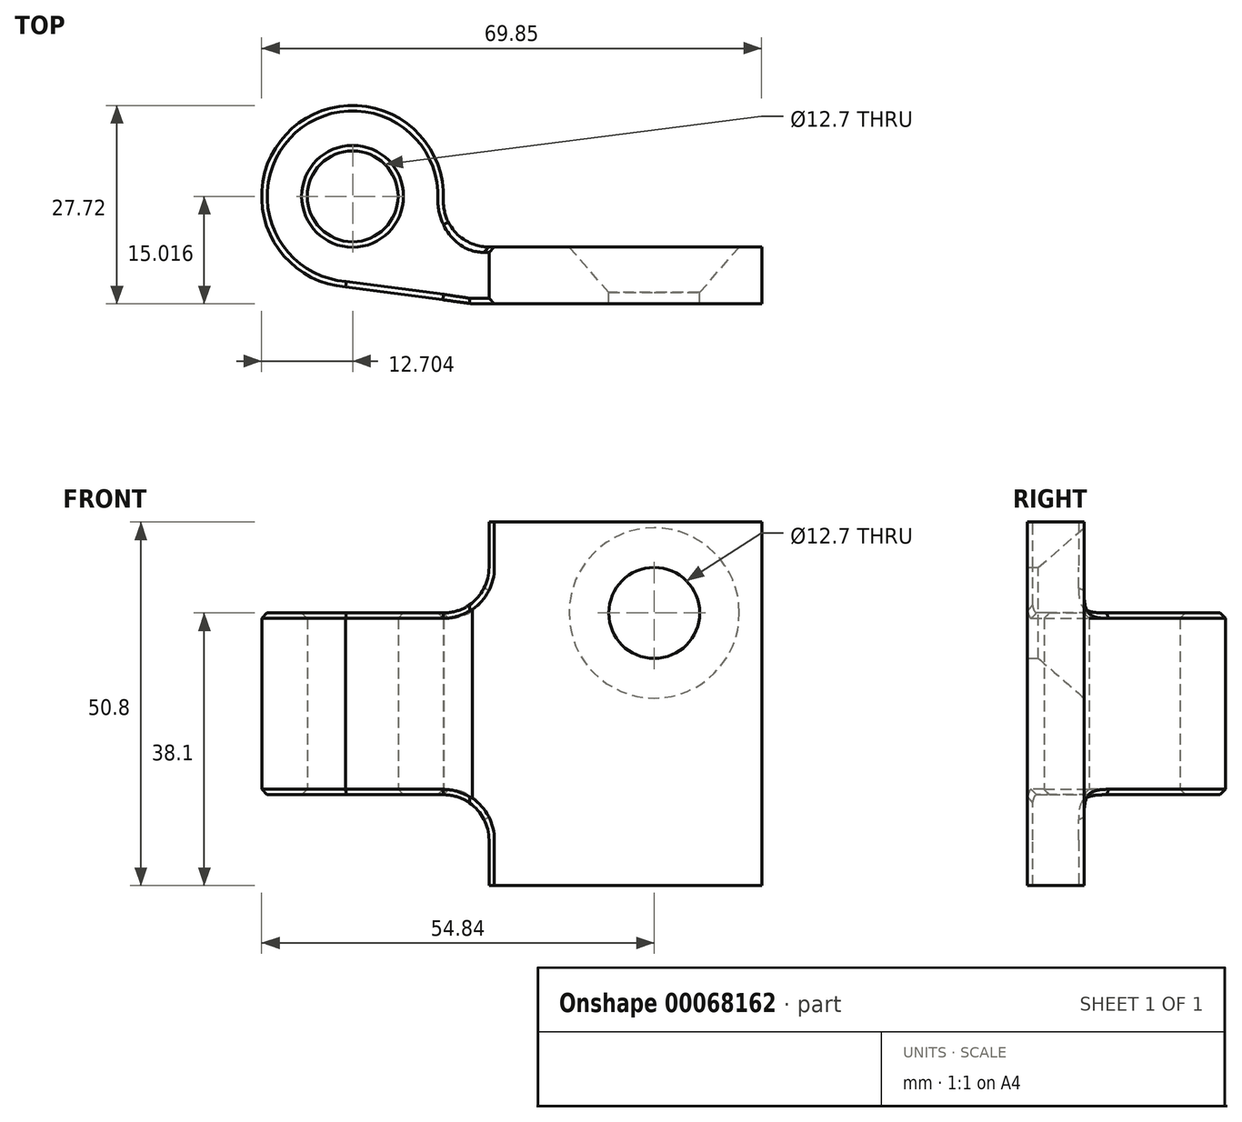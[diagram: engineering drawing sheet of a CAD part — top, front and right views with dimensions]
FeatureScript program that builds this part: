
annotation { "Feature Type Name" : "Feature", "Feature Type Description" : "" }
export const myFeature = defineFeature(function(context is Context, id is Id, definition is map)
    precondition{}
    {
        {
            var Q0;
            Q0=qCreatedBy(makeId("Front.planeOp"),FACE);
            var sketch = newSketch(context, id + "F0", { "sketchPlane" : qUnion([Q0])});
            skPoint(sketch, "E0.0", {"position": v(-63.5, 12.7) * mm});
            skCircle(sketch, "E1", {"center": v(-63.5, 12.7) * mm, "radius": 6.35 * mm});
            skCircle(sketch, "E2", {"center": v(0, 0) * mm, "radius": 88.9 * mm, "construction": true});
            skCircle(sketch, "E3.MirrorC", {"center": v(-63.5, -12.7) * mm, "radius": 6.35 * mm});
            skSolve(sketch);
        }
        {
            var Q0;
            Q0=qCreatedBy(makeId("Top.planeOp"),FACE);
            var sketch = newSketch(context, id + "F1", { "sketchPlane" : qUnion([Q0])});
            skLineSegment(sketch, "E4", {"start": v(-48.49, 0) * mm, "end": v(-88.9, 0) * mm});
            skCircle(sketch, "E5", {"center": v(-105.64, 5.63) * mm, "radius": 6.35 * mm});
            skArc(sketch, "E6.0", {"start": v(-92.95, 5.14) * mm, "mid": v(-114.09, 15.1) * mm, "end": v(-106.61, -7.04) * mm});
            skPoint(sketch, "E7.visualSharp", {"position": v(-94.25, 0) * mm});
            skPoint(sketch, "E8.visualSharp", {"position": v(-93.15, 7.94) * mm});
            skLineSegment(sketch, "E9.0", {"start": v(88.9, 0) * mm, "end": v(-88.9, 0) * mm});
            skLineSegment(sketch, "E10.0", {"start": v(-48.49, -9.39) * mm, "end": v(-88.9, -9.39) * mm});
            skLineSegment(sketch, "E11.0", {"start": v(-48.49, -1.45) * mm, "end": v(-86.6, -1.45) * mm});
            skArc(sketch, "E12.filletArc", {"start": v(-92.95, 5.14) * mm, "mid": v(-91.17, 0.5) * mm, "end": v(-86.6, -1.45) * mm});
            skLineSegment(sketch, "E13", {"start": v(-88.9, -9.39) * mm, "end": v(-106.61, -7.04) * mm});
            skLineSegment(sketch, "E14", {"start": v(-48.49, -1.45) * mm, "end": v(-48.49, -9.39) * mm});
            skSolve(sketch);
        }
        {
            var Q0;
            Q0=qCreatedBy(makeId("Front.planeOp"),FACE);
            cPlane(context, id + "F2", {"entities" : qUnion([Q0]), "cplaneType" : CPlaneType.OFFSET, "offset" : 25.4 * mm, "width" : 152.4 * mm, "height" : 152.4 * mm});
        }
        {
            var Q0;
            Q0=qCreatedBy(id+"F2.planeOp",FACE);
            var sketch = newSketch(context, id + "F3", { "sketchPlane" : qUnion([Q0])});
            skLineSegment(sketch, "E15.bottom", {"start": v(-118.34, 12.7) * mm, "end": v(-86.59, 12.7) * mm});
            skLineSegment(sketch, "E16.top", {"start": v(-118.34, 25.4) * mm, "end": v(-86.59, 25.4) * mm});
            skLineSegment(sketch, "E16.left", {"start": v(-118.34, 12.7) * mm, "end": v(-118.34, 25.4) * mm});
            skLineSegment(sketch, "E17.MirrorCS", {"start": v(-118.34, -12.7) * mm, "end": v(-86.59, -12.7) * mm});
            skLineSegment(sketch, "E18.MirrorCS", {"start": v(-118.34, -25.4) * mm, "end": v(-86.59, -25.4) * mm});
            skLineSegment(sketch, "E19.MirrorCS", {"start": v(-118.34, -12.7) * mm, "end": v(-118.34, -25.4) * mm});
            skLineSegment(sketch, "E20", {"start": v(-86.59, 25.4) * mm, "end": v(-86.59, 12.7) * mm});
            skLineSegment(sketch, "E21", {"start": v(-86.59, -12.7) * mm, "end": v(-86.59, -25.4) * mm});
            skSolve(sketch);
        }
        {
            var Q0;
            Q0=makeQuery(id+"F1.imprint","IMPRINT",FACE,{"disambiguationData":[TD([[makeQuery(id+"F1.imprint","IMPRINT",EDGE,{"derivedFrom":sQuery(id+"F1.wireOp",EDGE,"E5")}),-1.0]])]});
            extrude(context, id + "F4", {"entities" : qUnion([Q0]), "endBound" : BoundingType.SYMMETRIC, "depth" : 50.8 * mm});
        }
        {
            var Q0;
            Q0=makeQuery(id+"F3.imprint","IMPRINT",FACE,{"disambiguationData":[TD([[makeQuery(id+"F3.imprint","IMPRINT",EDGE,{"derivedFrom":sQuery(id+"F3.wireOp",EDGE,"E15.bottom")}),1.0]])]});
            var Q1;
            Q1=makeQuery(id+"F3.imprint","IMPRINT",FACE,{"disambiguationData":[TD([[makeQuery(id+"F3.imprint","IMPRINT",EDGE,{"derivedFrom":sQuery(id+"F3.wireOp",EDGE,"E17.MirrorCS")}),-1.0]])]});
            extrude(context, id + "F5", {"entities" : qUnion([Q0, Q1]), "operationType" : NewBodyOperationType.REMOVE, "endBound" : BoundingType.THROUGH_ALL, "oppositeDirection" : true, "depth" : 25.4 * mm});
        }
        {
            var Q0;
            Q0=makeQuery(id+"F0.imprint","IMPRINT",FACE,{"disambiguationData":[TD([[makeQuery(id+"F0.imprint","IMPRINT",EDGE,{"derivedFrom":sQuery(id+"F0.wireOp",EDGE,"E1")}),1.0]])]});
            var Q1;
            Q1=makeQuery(id+"F0.imprint","IMPRINT",FACE,{"disambiguationData":[TD([[makeQuery(id+"F0.imprint","IMPRINT",EDGE,{"derivedFrom":sQuery(id+"F0.wireOp",EDGE,"E3.MirrorC")}),-1.0]])]});
            extrude(context, id + "F6", {"entities" : qUnion([Q0, Q1]), "operationType" : NewBodyOperationType.REMOVE, "endBound" : BoundingType.THROUGH_ALL, "depth" : 25.4 * mm});
        }
        {
            var Q0;
            Q0=makeQuery(id+"F6.boolean.opBoolean","INTERSECT",EDGE,{"derivedFrom":[makeQuery(id+"F4.opExtrude","SWEPT_FACE",FACE,{"disambiguationData":[OSD([sQuery(id+"F1.wireOp",EDGE,"E11.0")])]}),makeQuery(id+"F6.opExtrude","SWEPT_FACE",FACE,{"disambiguationData":[OSD([sQuery(id+"F0.wireOp",EDGE,"E1")])]})]});
            var Q1;
            Q1=makeQuery(id+"F6.boolean.opBoolean","INTERSECT",EDGE,{"derivedFrom":[makeQuery(id+"F4.opExtrude","SWEPT_FACE",FACE,{"disambiguationData":[OSD([sQuery(id+"F1.wireOp",EDGE,"E11.0")])]}),makeQuery(id+"F6.opExtrude","SWEPT_FACE",FACE,{"disambiguationData":[OSD([sQuery(id+"F0.wireOp",EDGE,"E3.MirrorC")])]})]});
            chamfer(context, id + "F7", {"entities" : qUnion([Q0, Q1]), "chamferType" : ChamferType.OFFSET_ANGLE, "width" : 6.38 * mm, "oppositeDirection" : false, "angle" : 41 * degree, "tangentPropagation" : true});
        }
        {
            var Q0;
            Q0=makeQuery(id+"F5.boolean.opBoolean","COPY",EDGE,{"derivedFrom":makeQuery(id+"F5.opExtrude","SWEPT_EDGE",EDGE,{"disambiguationData":[OSD([sQuery(id+"F3.wireOp",EDGE,"E15.bottom"),sQuery(id+"F3.wireOp",EDGE,"E20")])]})});
            var Q1;
            Q1=makeQuery(id+"F5.boolean.opBoolean","COPY",EDGE,{"derivedFrom":makeQuery(id+"F5.opExtrude","SWEPT_EDGE",EDGE,{"disambiguationData":[OSD([sQuery(id+"F3.wireOp",EDGE,"E17.MirrorCS"),sQuery(id+"F3.wireOp",EDGE,"E21")])]})});
            fillet(context, id + "F8", {"entities" : qUnion([Q0, Q1]), "radius" : 6.35 * mm, "tangentPropagation" : true, "allowEdgeOverflow" : false});
        }
        {
            var Q0;
            Q0=makeQuery(id+"F8.opFillet","BLEND_EDGE",EDGE,{"blendedFrom":[makeQuery(id+"F5.boolean.opBoolean","COPY",EDGE,{"derivedFrom":makeQuery(id+"F5.opExtrude","SWEPT_EDGE",EDGE,{"disambiguationData":[OSD([sQuery(id+"F3.wireOp",EDGE,"E15.bottom"),sQuery(id+"F3.wireOp",EDGE,"E20")])]})}),makeQuery(id+"F4.opExtrude","SWEPT_FACE",FACE,{"disambiguationData":[OSD([sQuery(id+"F1.wireOp",EDGE,"E12.filletArc")])]})],"blendedInto":[makeQuery(id+"F4.opExtrude","SWEPT_FACE",FACE,{"disambiguationData":[OSD([sQuery(id+"F1.wireOp",EDGE,"E12.filletArc")])]})]});
            var Q1;
            Q1=makeQuery(id+"F5.boolean.opBoolean","INTERSECT",EDGE,{"derivedFrom":[makeQuery(id+"F4.opExtrude","SWEPT_FACE",FACE,{"disambiguationData":[OSD([sQuery(id+"F1.wireOp",EDGE,"E11.0")])]}),makeQuery(id+"F5.opExtrude","SWEPT_FACE",FACE,{"disambiguationData":[OSD([sQuery(id+"F3.wireOp",EDGE,"E20")])]})]});
            var Q2;
            Q2=makeQuery(id+"F5.boolean.opBoolean","INTERSECT",EDGE,{"derivedFrom":[makeQuery(id+"F4.opExtrude","SWEPT_FACE",FACE,{"disambiguationData":[OSD([sQuery(id+"F1.wireOp",EDGE,"E11.0")])]}),makeQuery(id+"F5.opExtrude","SWEPT_FACE",FACE,{"disambiguationData":[OSD([sQuery(id+"F3.wireOp",EDGE,"E21")])]})]});
            var Q3;
            Q3=makeQuery(id+"F8.opFillet","BLEND_EDGE",EDGE,{"blendedFrom":[makeQuery(id+"F5.boolean.opBoolean","COPY",EDGE,{"derivedFrom":makeQuery(id+"F5.opExtrude","SWEPT_EDGE",EDGE,{"disambiguationData":[OSD([sQuery(id+"F3.wireOp",EDGE,"E17.MirrorCS"),sQuery(id+"F3.wireOp",EDGE,"E21")])]})}),makeQuery(id+"F4.opExtrude","SWEPT_FACE",FACE,{"disambiguationData":[OSD([sQuery(id+"F1.wireOp",EDGE,"E12.filletArc")])]})],"blendedInto":[makeQuery(id+"F4.opExtrude","SWEPT_FACE",FACE,{"disambiguationData":[OSD([sQuery(id+"F1.wireOp",EDGE,"E12.filletArc")])]})]});
            var Q4;
            Q4=makeQuery(id+"F5.boolean.opBoolean","INTERSECT",EDGE,{"derivedFrom":[makeQuery(id+"F4.opExtrude","SWEPT_FACE",FACE,{"disambiguationData":[OSD([sQuery(id+"F1.wireOp",EDGE,"E6.0")])]}),makeQuery(id+"F5.opExtrude","SWEPT_FACE",FACE,{"disambiguationData":[OSD([sQuery(id+"F3.wireOp",EDGE,"E17.MirrorCS")])]})]});
            var Q5;
            Q5=makeQuery(id+"F5.boolean.opBoolean","INTERSECT",EDGE,{"derivedFrom":[makeQuery(id+"F4.opExtrude","SWEPT_FACE",FACE,{"disambiguationData":[OSD([sQuery(id+"F1.wireOp",EDGE,"E13")])]}),makeQuery(id+"F5.opExtrude","SWEPT_FACE",FACE,{"disambiguationData":[OSD([sQuery(id+"F3.wireOp",EDGE,"E17.MirrorCS")])]})]});
            var Q6;
            Q6=makeQuery(id+"F5.boolean.opBoolean","INTERSECT",EDGE,{"derivedFrom":[makeQuery(id+"F4.opExtrude","SWEPT_FACE",FACE,{"disambiguationData":[OSD([sQuery(id+"F1.wireOp",EDGE,"E12.filletArc")])]}),makeQuery(id+"F5.opExtrude","SWEPT_FACE",FACE,{"disambiguationData":[OSD([sQuery(id+"F3.wireOp",EDGE,"E17.MirrorCS")])]})]});
            var Q7;
            Q7=makeQuery(id+"F8.opFillet","BLEND_EDGE",EDGE,{"blendedFrom":[makeQuery(id+"F5.boolean.opBoolean","COPY",EDGE,{"derivedFrom":makeQuery(id+"F5.opExtrude","SWEPT_EDGE",EDGE,{"disambiguationData":[OSD([sQuery(id+"F3.wireOp",EDGE,"E17.MirrorCS"),sQuery(id+"F3.wireOp",EDGE,"E21")])]})}),makeQuery(id+"F4.opExtrude","SWEPT_FACE",FACE,{"disambiguationData":[OSD([sQuery(id+"F1.wireOp",EDGE,"E13")])]})],"blendedInto":[makeQuery(id+"F4.opExtrude","SWEPT_FACE",FACE,{"disambiguationData":[OSD([sQuery(id+"F1.wireOp",EDGE,"E13")])]})]});
            var Q8;
            Q8=makeQuery(id+"F5.boolean.opBoolean","INTERSECT",EDGE,{"derivedFrom":[makeQuery(id+"F4.opExtrude","SWEPT_FACE",FACE,{"disambiguationData":[OSD([sQuery(id+"F1.wireOp",EDGE,"E10.0")])]}),makeQuery(id+"F5.opExtrude","SWEPT_FACE",FACE,{"disambiguationData":[OSD([sQuery(id+"F3.wireOp",EDGE,"E21")])]})]});
            var Q9;
            Q9=makeQuery(id+"F8.opFillet","BLEND_EDGE",EDGE,{"blendedFrom":[makeQuery(id+"F5.boolean.opBoolean","COPY",EDGE,{"derivedFrom":makeQuery(id+"F5.opExtrude","SWEPT_EDGE",EDGE,{"disambiguationData":[OSD([sQuery(id+"F3.wireOp",EDGE,"E15.bottom"),sQuery(id+"F3.wireOp",EDGE,"E20")])]})}),makeQuery(id+"F4.opExtrude","SWEPT_FACE",FACE,{"disambiguationData":[OSD([sQuery(id+"F1.wireOp",EDGE,"E10.0")])]})],"blendedInto":[makeQuery(id+"F4.opExtrude","SWEPT_FACE",FACE,{"disambiguationData":[OSD([sQuery(id+"F1.wireOp",EDGE,"E10.0")])]})]});
            var Q10;
            Q10=makeQuery(id+"F5.boolean.opBoolean","INTERSECT",EDGE,{"derivedFrom":[makeQuery(id+"F4.opExtrude","SWEPT_FACE",FACE,{"disambiguationData":[OSD([sQuery(id+"F1.wireOp",EDGE,"E10.0")])]}),makeQuery(id+"F5.opExtrude","SWEPT_FACE",FACE,{"disambiguationData":[OSD([sQuery(id+"F3.wireOp",EDGE,"E20")])]})]});
            var Q11;
            Q11=makeQuery(id+"F8.opFillet","BLEND_EDGE",EDGE,{"blendedFrom":[makeQuery(id+"F5.boolean.opBoolean","COPY",EDGE,{"derivedFrom":makeQuery(id+"F5.opExtrude","SWEPT_EDGE",EDGE,{"disambiguationData":[OSD([sQuery(id+"F3.wireOp",EDGE,"E15.bottom"),sQuery(id+"F3.wireOp",EDGE,"E20")])]})}),makeQuery(id+"F4.opExtrude","SWEPT_FACE",FACE,{"disambiguationData":[OSD([sQuery(id+"F1.wireOp",EDGE,"E13")])]})],"blendedInto":[makeQuery(id+"F4.opExtrude","SWEPT_FACE",FACE,{"disambiguationData":[OSD([sQuery(id+"F1.wireOp",EDGE,"E13")])]})]});
            var Q12;
            Q12=makeQuery(id+"F5.boolean.opBoolean","INTERSECT",EDGE,{"derivedFrom":[makeQuery(id+"F4.opExtrude","SWEPT_FACE",FACE,{"disambiguationData":[OSD([sQuery(id+"F1.wireOp",EDGE,"E13")])]}),makeQuery(id+"F5.opExtrude","SWEPT_FACE",FACE,{"disambiguationData":[OSD([sQuery(id+"F3.wireOp",EDGE,"E15.bottom")])]})]});
            var Q13;
            Q13=makeQuery(id+"F5.boolean.opBoolean","INTERSECT",EDGE,{"derivedFrom":[makeQuery(id+"F4.opExtrude","SWEPT_FACE",FACE,{"disambiguationData":[OSD([sQuery(id+"F1.wireOp",EDGE,"E6.0")])]}),makeQuery(id+"F5.opExtrude","SWEPT_FACE",FACE,{"disambiguationData":[OSD([sQuery(id+"F3.wireOp",EDGE,"E15.bottom")])]})]});
            var Q14;
            Q14=makeQuery(id+"F5.boolean.opBoolean","INTERSECT",EDGE,{"derivedFrom":[makeQuery(id+"F4.opExtrude","SWEPT_FACE",FACE,{"disambiguationData":[OSD([sQuery(id+"F1.wireOp",EDGE,"E12.filletArc")])]}),makeQuery(id+"F5.opExtrude","SWEPT_FACE",FACE,{"disambiguationData":[OSD([sQuery(id+"F3.wireOp",EDGE,"E15.bottom")])]})]});
            var Q15;
            Q15=makeQuery(id+"F8.opFillet","BLEND_EDGE",EDGE,{"blendedFrom":[makeQuery(id+"F5.boolean.opBoolean","COPY",EDGE,{"derivedFrom":makeQuery(id+"F5.opExtrude","SWEPT_EDGE",EDGE,{"disambiguationData":[OSD([sQuery(id+"F3.wireOp",EDGE,"E15.bottom"),sQuery(id+"F3.wireOp",EDGE,"E20")])]})}),makeQuery(id+"F4.opExtrude","SWEPT_FACE",FACE,{"disambiguationData":[OSD([sQuery(id+"F1.wireOp",EDGE,"E11.0")])]})],"blendedInto":[makeQuery(id+"F4.opExtrude","SWEPT_FACE",FACE,{"disambiguationData":[OSD([sQuery(id+"F1.wireOp",EDGE,"E11.0")])]})]});
            var Q16;
            Q16=makeQuery(id+"F8.opFillet","BLEND_EDGE",EDGE,{"blendedFrom":[makeQuery(id+"F5.boolean.opBoolean","COPY",EDGE,{"derivedFrom":makeQuery(id+"F5.opExtrude","SWEPT_EDGE",EDGE,{"disambiguationData":[OSD([sQuery(id+"F3.wireOp",EDGE,"E17.MirrorCS"),sQuery(id+"F3.wireOp",EDGE,"E21")])]})}),makeQuery(id+"F4.opExtrude","SWEPT_FACE",FACE,{"disambiguationData":[OSD([sQuery(id+"F1.wireOp",EDGE,"E10.0")])]})],"blendedInto":[makeQuery(id+"F4.opExtrude","SWEPT_FACE",FACE,{"disambiguationData":[OSD([sQuery(id+"F1.wireOp",EDGE,"E10.0")])]})]});
            var Q17;
            Q17=makeQuery(id+"F8.opFillet","BLEND_EDGE",EDGE,{"blendedFrom":[makeQuery(id+"F5.boolean.opBoolean","COPY",EDGE,{"derivedFrom":makeQuery(id+"F5.opExtrude","SWEPT_EDGE",EDGE,{"disambiguationData":[OSD([sQuery(id+"F3.wireOp",EDGE,"E17.MirrorCS"),sQuery(id+"F3.wireOp",EDGE,"E21")])]})}),makeQuery(id+"F4.opExtrude","SWEPT_FACE",FACE,{"disambiguationData":[OSD([sQuery(id+"F1.wireOp",EDGE,"E11.0")])]})],"blendedInto":[makeQuery(id+"F4.opExtrude","SWEPT_FACE",FACE,{"disambiguationData":[OSD([sQuery(id+"F1.wireOp",EDGE,"E11.0")])]})]});
            var Q18;
            Q18=makeQuery(id+"F5.boolean.opBoolean","INTERSECT",EDGE,{"derivedFrom":[makeQuery(id+"F4.opExtrude","SWEPT_FACE",FACE,{"disambiguationData":[OSD([sQuery(id+"F1.wireOp",EDGE,"E5")])]}),makeQuery(id+"F5.opExtrude","SWEPT_FACE",FACE,{"disambiguationData":[OSD([sQuery(id+"F3.wireOp",EDGE,"E15.bottom")])]})]});
            var Q19;
            Q19=makeQuery(id+"F5.boolean.opBoolean","INTERSECT",EDGE,{"derivedFrom":[makeQuery(id+"F4.opExtrude","SWEPT_FACE",FACE,{"disambiguationData":[OSD([sQuery(id+"F1.wireOp",EDGE,"E5")])]}),makeQuery(id+"F5.opExtrude","SWEPT_FACE",FACE,{"disambiguationData":[OSD([sQuery(id+"F3.wireOp",EDGE,"E17.MirrorCS")])]})]});
            var Q20;
            Q20=makeQuery(id+"F5.boolean.opBoolean","COPY",EDGE,{"derivedFrom":makeQuery(id+"F5.opExtrude","SWEPT_EDGE",EDGE,{"disambiguationData":[OSD([sQuery(id+"F3.wireOp",EDGE,"E18.MirrorCS"),sQuery(id+"F3.wireOp",EDGE,"E21")])]})});
            var Q21;
            Q21=makeQuery(id+"F5.boolean.opBoolean","COPY",EDGE,{"derivedFrom":makeQuery(id+"F5.opExtrude","SWEPT_EDGE",EDGE,{"disambiguationData":[OSD([sQuery(id+"F3.wireOp",EDGE,"E16.top"),sQuery(id+"F3.wireOp",EDGE,"E20")])]})});
            chamfer(context, id + "F9", {"entities" : qUnion([Q0, Q1, Q2, Q3, Q4, Q5, Q6, Q7, Q8, Q9, Q10, Q11, Q12, Q13, Q14, Q15, Q16, Q17, Q18, Q19, Q20, Q21]), "width" : 0.76 * mm});
        }
    });
